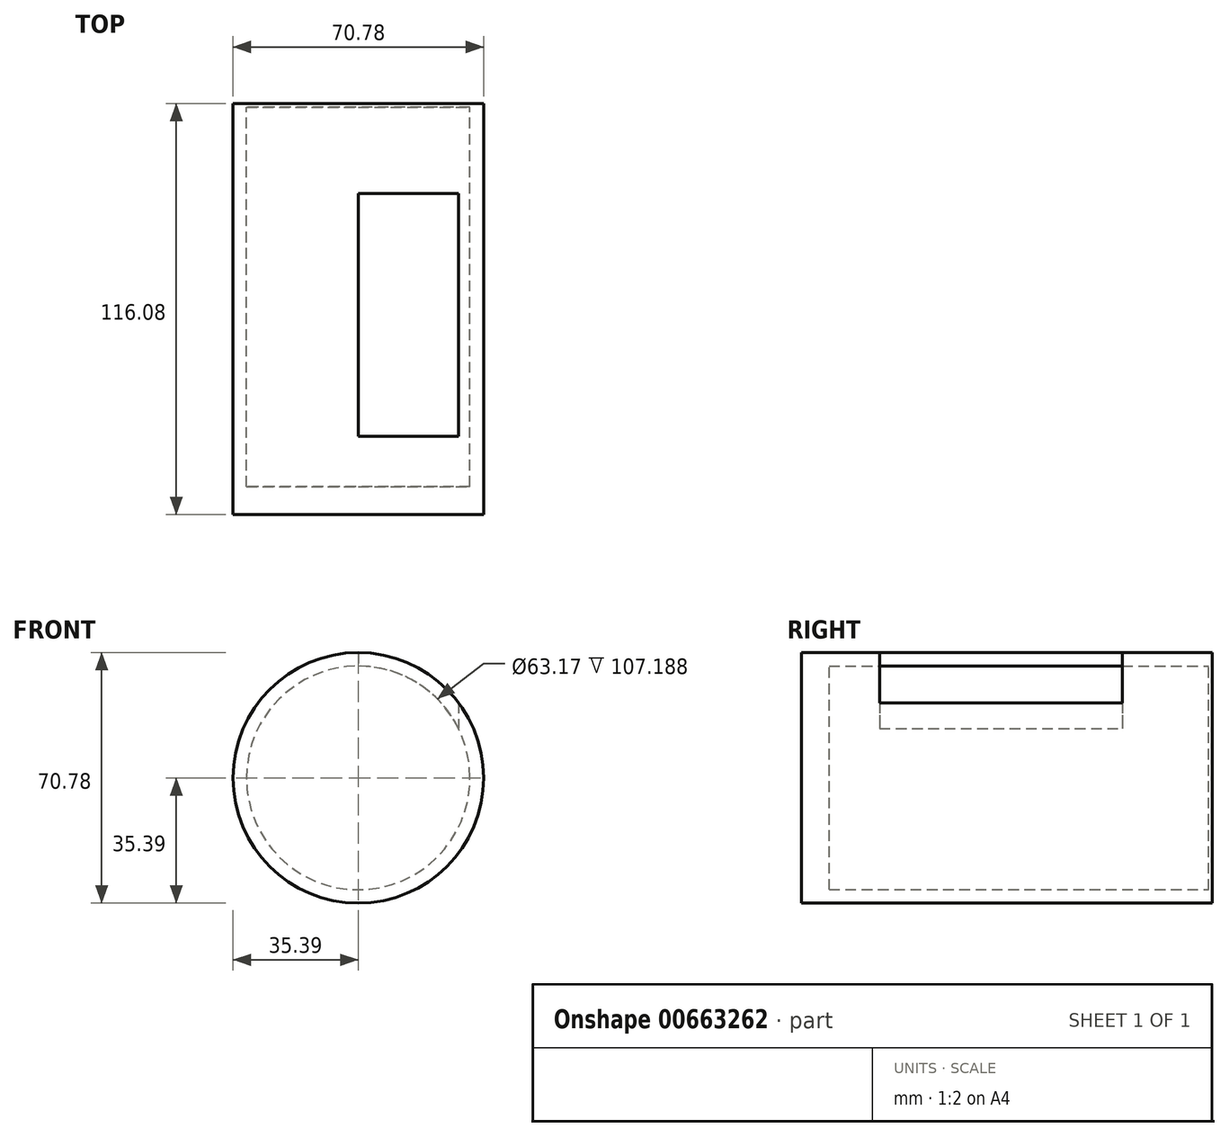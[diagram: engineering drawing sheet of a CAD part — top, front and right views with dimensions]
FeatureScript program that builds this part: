
annotation { "Feature Type Name" : "Feature", "Feature Type Description" : "" }
export const myFeature = defineFeature(function(context is Context, id is Id, definition is map)
    precondition{}
    {
        {
            var Q0;
            Q0=qCreatedBy(makeId("Front.planeOp"),FACE);
            var sketch = newSketch(context, id + "F0", { "sketchPlane" : qUnion([Q0])});
            skCircle(sketch, "E0", {"center": v(0, 0) * mm, "radius": 35.4 * mm});
            skSolve(sketch);
        }
        {
            var Q0;
            Q0=makeQuery(id+"F0.imprint","IMPRINT",FACE,{"disambiguationData":[TD([[makeQuery(id+"F0.imprint","IMPRINT",EDGE,{"derivedFrom":sQuery(id+"F0.wireOp",EDGE,"E0")}),1.0]])]});
            extrude(context, id + "F1", {"entities" : qUnion([Q0]), "depth" : 116.08 * mm, "offsetDistance" : 25.4 * mm});
        }
        {
            var Q0;
            Q0=qCreatedBy(makeId("Front.planeOp"),FACE);
            var sketch = newSketch(context, id + "F2", { "sketchPlane" : qUnion([Q0])});
            skCircle(sketch, "E1", {"center": v(0, 0) * mm, "radius": 31.58 * mm});
            skSolve(sketch);
        }
        {
            var Q0;
            Q0 = qSketchRegion(id + "F2", true);
            extrude(context, id + "F3", {"entities" : qUnion([Q0]), "operationType" : NewBodyOperationType.REMOVE, "depth" : 108.2 * mm, "offsetDistance" : 25.4 * mm});
        }
        {
            var Q0;
            Q0 = qSketchRegion(id + "F2", true);
            extrude(context, id + "F4", {"entities" : qUnion([Q0]), "operationType" : NewBodyOperationType.ADD, "depth" : 1.02 * mm, "offsetDistance" : 25.4 * mm});
        }
        {
            var Q0;
            Q0=qCreatedBy(makeId("Top.planeOp"),FACE);
            var sketch = newSketch(context, id + "F5", { "sketchPlane" : qUnion([Q0])});
            skLineSegment(sketch, "E2.bottom", {"start": v(0, -25.41) * mm, "end": v(28.33, -25.41) * mm});
            skLineSegment(sketch, "E2.top", {"start": v(0, -93.97) * mm, "end": v(28.33, -93.97) * mm});
            skLineSegment(sketch, "E2.left", {"start": v(0, -25.41) * mm, "end": v(0, -93.97) * mm});
            skLineSegment(sketch, "E2.right", {"start": v(28.33, -25.41) * mm, "end": v(28.33, -93.97) * mm});
            skSolve(sketch);
        }
        {
            var Q0;
            Q0 = qSketchRegion(id + "F5", true);
            extrude(context, id + "F6", {"entities" : qUnion([Q0]), "operationType" : NewBodyOperationType.REMOVE, "depth" : 66.7 * mm, "offsetDistance" : 25 * mm});
        }
    });
